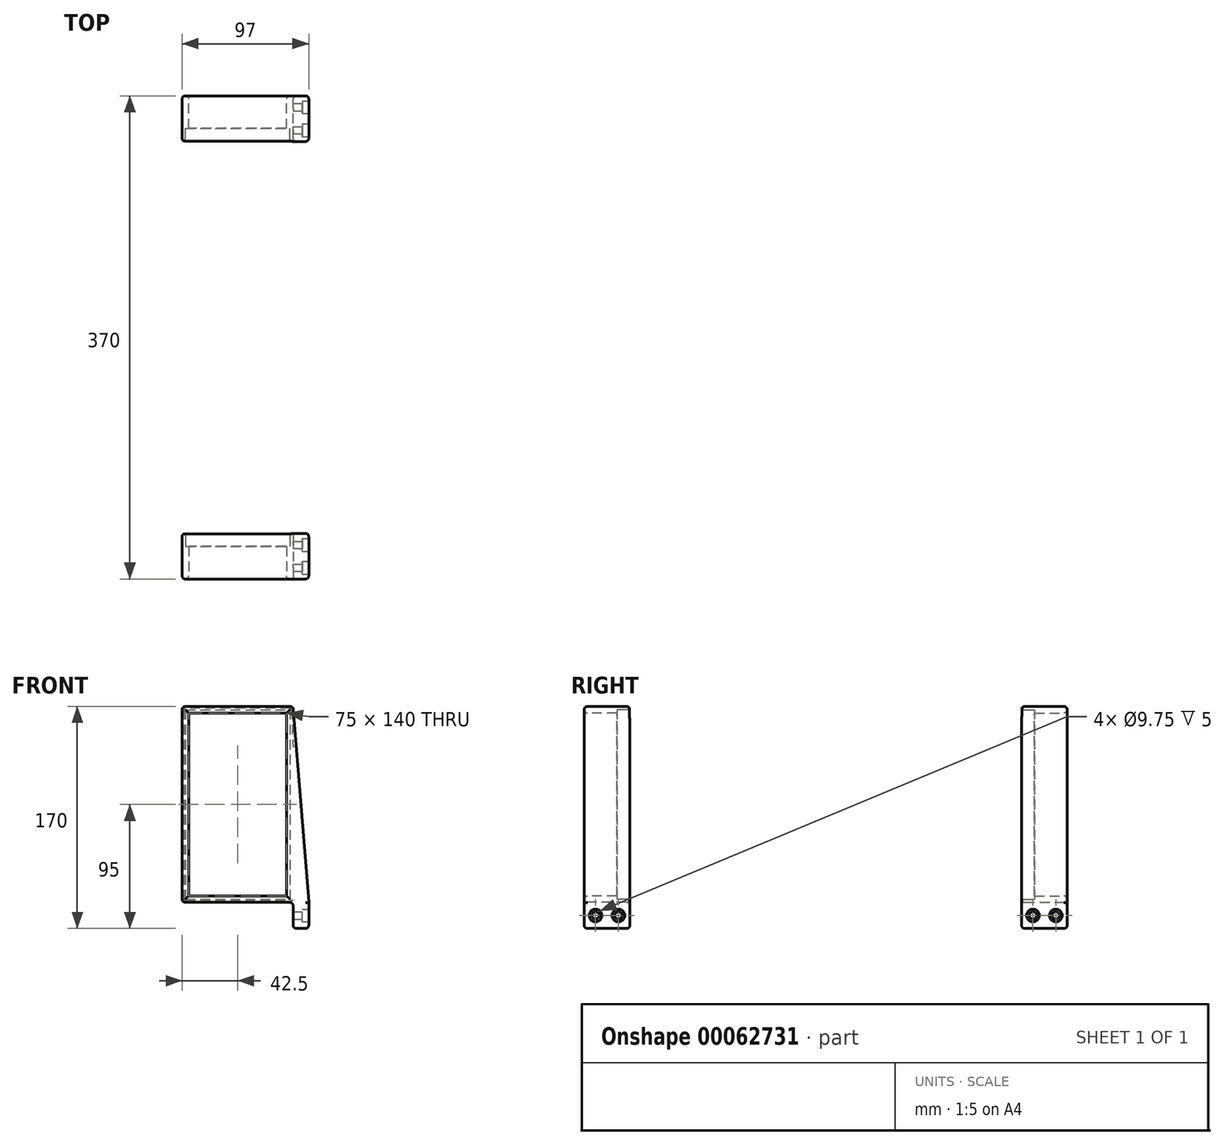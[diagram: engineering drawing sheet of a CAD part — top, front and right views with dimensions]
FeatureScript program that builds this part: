
annotation { "Feature Type Name" : "Feature", "Feature Type Description" : "" }
export const myFeature = defineFeature(function(context is Context, id is Id, definition is map)
    precondition{}
    {
        {
            var Q0;
            Q0=qCreatedBy(makeId("Front.planeOp"),FACE);
            var sketch = newSketch(context, id + "F0", { "sketchPlane" : qUnion([Q0])});
            skLineSegment(sketch, "E0.bottom", {"start": v(0, 0) * mm, "end": v(-85, 0) * mm});
            skLineSegment(sketch, "E0.top", {"start": v(0, 150) * mm, "end": v(-85, 150) * mm});
            skLineSegment(sketch, "E0.left", {"start": v(0, 0) * mm, "end": v(0, 150) * mm});
            skLineSegment(sketch, "E0.right", {"start": v(-85, 0) * mm, "end": v(-85, 150) * mm});
            skLineSegment(sketch, "E1.bottom", {"start": v(0, 0) * mm, "end": v(12, 0) * mm});
            skLineSegment(sketch, "E1.top", {"start": v(0, -20) * mm, "end": v(12, -20) * mm});
            skLineSegment(sketch, "E1.left", {"start": v(0, 0) * mm, "end": v(0, -20) * mm});
            skLineSegment(sketch, "E1.right", {"start": v(12, 0) * mm, "end": v(12, -20) * mm});
            skLineSegment(sketch, "E2", {"start": v(0, 150) * mm, "end": v(12, 0) * mm});
            skLineSegment(sketch, "E3", {"start": v(-85, 75) * mm, "end": v(0, 75) * mm, "construction": true});
            skLineSegment(sketch, "E4", {"start": v(0, 75) * mm, "end": v(0, 150) * mm, "construction": true});
            skPoint(sketch, "E5", {"position": v(-42.5, 112.5) * mm});
            skPoint(sketch, "E5.positionSnap0", {"position": v(-42.5, 75) * mm});
            skPoint(sketch, "E5.positionSnap1", {"position": v(0, 112.5) * mm});
            skPoint(sketch, "E6.MirrorP", {"position": v(-42.5, 37.5) * mm});
            skLineSegment(sketch, "E7.0", {"start": v(-5, 5) * mm, "end": v(-5, 145) * mm});
            skLineSegment(sketch, "E7.1", {"start": v(-5, 5) * mm, "end": v(-80, 5) * mm});
            skLineSegment(sketch, "E7.2", {"start": v(-80, 5) * mm, "end": v(-80, 145) * mm});
            skLineSegment(sketch, "E7.3", {"start": v(-5, 145) * mm, "end": v(-80, 145) * mm});
            skLineSegment(sketch, "E8", {"start": v(-42.5, 150) * mm, "end": v(-42.5, 0) * mm, "construction": true});
            skSolve(sketch);
        }
        {
            var Q0;
            Q0=makeQuery(id+"F0.imprint","IMPRINT",FACE,{"disambiguationData":[TD([[makeQuery(id+"F0.imprint","IMPRINT",EDGE,{"derivedFrom":sQuery(id+"F0.wireOp",EDGE,"E0.bottom")}),-1.0]])]});
            var Q1;
            Q1=makeQuery(id+"F0.imprint","IMPRINT",FACE,{"disambiguationData":[TD([[makeQuery(id+"F0.imprint","IMPRINT",EDGE,{"derivedFrom":sQuery(id+"F0.wireOp",EDGE,"E7.0")}),1.0]])]});
            extrude(context, id + "F1", {"entities" : qUnion([Q0, Q1]), "oppositeDirection" : true, "depth" : 35 * mm});
        }
        {
            var Q0;
            Q0=makeQuery(id+"F1.opExtrude","CAP_FACE",FACE,{"disambiguationData":[OSD([sQuery(id+"F0.wireOp",EDGE,"E0.bottom"),sQuery(id+"F0.wireOp",EDGE,"E0.top"),sQuery(id+"F0.wireOp",EDGE,"E0.right"),sQuery(id+"F0.wireOp",EDGE,"E1.top"),sQuery(id+"F0.wireOp",EDGE,"E1.left"),sQuery(id+"F0.wireOp",EDGE,"E1.right"),sQuery(id+"F0.wireOp",EDGE,"E2")])],"isStart":false});
            shell(context, id + "F2", {"entities" : qUnion([Q0]), "thickness" : 2.5 * mm});
        }
        {
            var Q0;
            Q0=makeQuery(id+"F0.imprint","IMPRINT",FACE,{"disambiguationData":[TD([[makeQuery(id+"F0.imprint","IMPRINT",EDGE,{"derivedFrom":sQuery(id+"F0.wireOp",EDGE,"E1.bottom")}),-1.0]])]});
            var Q1;
            Q1=makeQuery(id+"F0.imprint","IMPRINT",FACE,{"disambiguationData":[TD([[makeQuery(id+"F0.imprint","IMPRINT",EDGE,{"derivedFrom":sQuery(id+"F0.wireOp",EDGE,"E0.left")}),-1.0]])]});
            var Q2;
            Q2=makeQuery(id+"F1.opExtrude","CAP_FACE",FACE,{"disambiguationData":[OSD([sQuery(id+"F0.wireOp",EDGE,"E0.bottom"),sQuery(id+"F0.wireOp",EDGE,"E0.top"),sQuery(id+"F0.wireOp",EDGE,"E0.left"),sQuery(id+"F0.wireOp",EDGE,"E0.right")])],"isStart":false});
            extrude(context, id + "F3", {"entities" : qUnion([Q0, Q1]), "operationType" : NewBodyOperationType.ADD, "endBound" : BoundingType.UP_TO_SURFACE, "oppositeDirection" : true, "endBoundEntityFace" : qUnion([Q2]), "depth" : 25 * mm});
        }
        {
            var Q0;
            Q0=makeQuery(id+"F3.opExtrude","SWEPT_FACE",FACE,{"disambiguationData":[OSD([sQuery(id+"F0.wireOp",EDGE,"E1.right")])]});
            var sketch = newSketch(context, id + "F4", { "sketchPlane" : qUnion([Q0])});
            skLineSegment(sketch, "E9", {"start": v(17.5, 0) * mm, "end": v(17.5, -20) * mm, "construction": true});
            skLineSegment(sketch, "E10", {"start": v(17.5, -10) * mm, "end": v(35, -10) * mm, "construction": true});
            skLineSegment(sketch, "E11", {"start": v(17.5, -10) * mm, "end": v(0, -10) * mm, "construction": true});
            skPoint(sketch, "E12", {"position": v(8.75, -10) * mm});
            skPoint(sketch, "E13", {"position": v(26.25, -10) * mm});
            skSolve(sketch);
        }
        {
            var Q0;
            Q0=makeQuery(id+"F0.imprint","IMPRINT",FACE,{"disambiguationData":[TD([[makeQuery(id+"F0.imprint","IMPRINT",EDGE,{"derivedFrom":sQuery(id+"F0.wireOp",EDGE,"E0.bottom")}),-1.0]])]});
            extrude(context, id + "F5", {"entities" : qUnion([Q0]), "operationType" : NewBodyOperationType.ADD, "oppositeDirection" : true, "depth" : 25 * mm});
        }
        {
            var Q0;
            Q0=makeQuery(id+"F0.imprint","IMPRINT",FACE,{"disambiguationData":[TD([[makeQuery(id+"F0.imprint","IMPRINT",EDGE,{"derivedFrom":sQuery(id+"F0.wireOp",EDGE,"E7.0")}),1.0]])]});
            extrude(context, id + "F6", {"entities" : qUnion([Q0]), "operationType" : NewBodyOperationType.REMOVE, "endBound" : BoundingType.UP_TO_NEXT, "oppositeDirection" : true, "depth" : 25 * mm});
        }
        {
            var Q0;
            {var subQ0=sQuery(id+"F0.wireOp",EDGE,"E0.left");Q0=makeQuery(id+"F3.boolean.opBoolean","MERGE",FACE,{"derivedFrom":[makeQuery(id+"F1.opExtrude","CAP_FACE",FACE,{"disambiguationData":[OSD([sQuery(id+"F0.wireOp",EDGE,"E0.bottom"),sQuery(id+"F0.wireOp",EDGE,"E0.top"),subQ0,sQuery(id+"F0.wireOp",EDGE,"E0.right")])],"isStart":false}),makeQuery(id+"F3.opExtrude","CAP_FACE",FACE,{"disambiguationData":[OSD([subQ0,sQuery(id+"F0.wireOp",EDGE,"E1.top"),sQuery(id+"F0.wireOp",EDGE,"E1.left"),sQuery(id+"F0.wireOp",EDGE,"E1.right"),sQuery(id+"F0.wireOp",EDGE,"E2")])],"isStart":false})]});}
            var Q1;
            {var subQ0=sQuery(id+"F0.wireOp",EDGE,"E0.left");Q1=makeQuery(id+"F3.boolean.opBoolean","MERGE",FACE,{"derivedFrom":[makeQuery(id+"F1.opExtrude","CAP_FACE",FACE,{"disambiguationData":[OSD([sQuery(id+"F0.wireOp",EDGE,"E0.bottom"),sQuery(id+"F0.wireOp",EDGE,"E0.top"),subQ0,sQuery(id+"F0.wireOp",EDGE,"E0.right")])],"isStart":true}),makeQuery(id+"F3.opExtrude","CAP_FACE",FACE,{"disambiguationData":[OSD([subQ0,sQuery(id+"F0.wireOp",EDGE,"E1.top"),sQuery(id+"F0.wireOp",EDGE,"E1.left"),sQuery(id+"F0.wireOp",EDGE,"E1.right"),sQuery(id+"F0.wireOp",EDGE,"E2")])],"isStart":true})]});}
            var Q2;
            Q2=makeQuery(id+"F1.opExtrude","SWEPT_FACE",FACE,{"disambiguationData":[OSD([sQuery(id+"F0.wireOp",EDGE,"E0.top")])]});
            var Q3;
            Q3=makeQuery(id+"F1.opExtrude","SWEPT_FACE",FACE,{"disambiguationData":[OSD([sQuery(id+"F0.wireOp",EDGE,"E0.bottom")])]});
            var Q4;
            Q4=makeQuery(id+"F3.opExtrude","SWEPT_FACE",FACE,{"disambiguationData":[OSD([sQuery(id+"F0.wireOp",EDGE,"E1.right")])]});
            var Q5;
            Q5=makeQuery(id+"F3.opExtrude","SWEPT_FACE",FACE,{"disambiguationData":[OSD([sQuery(id+"F0.wireOp",EDGE,"E2")])]});
            var Q6;
            Q6=makeQuery(id+"F1.opExtrude","SWEPT_FACE",FACE,{"disambiguationData":[OSD([sQuery(id+"F0.wireOp",EDGE,"E0.right")])]});
            var Q7;
            Q7=makeQuery(id+"F3.opExtrude","SWEPT_FACE",FACE,{"disambiguationData":[OSD([sQuery(id+"F0.wireOp",EDGE,"E0.left"),sQuery(id+"F0.wireOp",EDGE,"E1.left")])]});
            fillet(context, id + "F7", {"entities" : qUnion([Q0, Q1, Q2, Q3, Q4, Q5, Q6, Q7]), "radius" : 2.5 * mm, "tangentPropagation" : true, "allowEdgeOverflow" : false});
        }
        {
            var Q0;
            Q0=sQuery(id+"F4.wireOp",VERTEX,"E13");
            var Q1;
            Q1=sQuery(id+"F4.wireOp",VERTEX,"E12");
            var Q2;
            Q2=makeQuery(id+"F1.opExtrude","SWEPT_BODY",BODY,{"disambiguationData":[OSD([sQuery(id+"F0.wireOp",EDGE,"E0.bottom"),sQuery(id+"F0.wireOp",EDGE,"E0.top"),sQuery(id+"F0.wireOp",EDGE,"E0.left"),sQuery(id+"F0.wireOp",EDGE,"E0.right")])]});
            hole(context, id + "F8", {"style" : HoleStyle.C_BORE, "endStyle" : HoleEndStyle.THROUGH, "standardTappedOrClearance" : lookupTablePath({ "standard" : "ISO", "fit" : "Normal", "size" : "M5", "type" : "Clearance" }), "standardBlindInLast" : lookupTablePath({ "fit" : "Standard", "standard" : "ISO", "size" : "M5", "type" : "Clearance" }), "holeDiameter" : 5.5 * mm, "cBoreDiameter" : 9.75 * mm, "cBoreDepth" : 5 * mm, "locations" : qUnion([Q0, Q1]), "scope" : qUnion([Q2]), "isTappedThrough" : true});
        }
        {
            var Q0;
            {var subQ0=sQuery(id+"F0.wireOp",EDGE,"E0.left");Q0=makeQuery(id+"F3.boolean.opBoolean","MERGE",FACE,{"derivedFrom":[makeQuery(id+"F1.opExtrude","CAP_FACE",FACE,{"disambiguationData":[OSD([sQuery(id+"F0.wireOp",EDGE,"E0.bottom"),sQuery(id+"F0.wireOp",EDGE,"E0.top"),subQ0,sQuery(id+"F0.wireOp",EDGE,"E0.right")])],"isStart":false}),makeQuery(id+"F3.opExtrude","CAP_FACE",FACE,{"disambiguationData":[OSD([subQ0,sQuery(id+"F0.wireOp",EDGE,"E1.top"),sQuery(id+"F0.wireOp",EDGE,"E1.left"),sQuery(id+"F0.wireOp",EDGE,"E1.right"),sQuery(id+"F0.wireOp",EDGE,"E2")])],"isStart":false})]});}
            cPlane(context, id + "F9", {"entities" : qUnion([Q0]), "cplaneType" : CPlaneType.OFFSET, "offset" : 150 * mm, "width" : 150 * mm, "height" : 150 * mm});
        }
        {
            var Q0;
            Q0=makeQuery(id+"F1.opExtrude","SWEPT_BODY",BODY,{"disambiguationData":[OSD([sQuery(id+"F0.wireOp",EDGE,"E0.bottom"),sQuery(id+"F0.wireOp",EDGE,"E0.top"),sQuery(id+"F0.wireOp",EDGE,"E0.left"),sQuery(id+"F0.wireOp",EDGE,"E0.right")])]});
            var Q1;
            Q1=qCreatedBy(id+"F9.planeOp",FACE);
            mirror(context, id + "F10", {"entities" : qUnion([Q0]), "mirrorPlane" : qUnion([Q1])});
        }
    });
